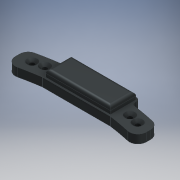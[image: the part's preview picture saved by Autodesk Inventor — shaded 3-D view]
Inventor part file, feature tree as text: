
AUTODESK INVENTOR PART (.ipt)
format: ipt  version: 2018 (Build 220112000, 112)  size: 166,400 bytes
history: native  units: mm
features: extrude x2, sketch x2, hole x1, mirror x1, fillet x1
ambient origin geometry x8: Origin, YZ Plane, XZ Plane, XY Plane, X Axis, Y Axis, Z Axis, Center Point
bodies: Solid1 (feature_tree)
feature tree (7):
  extrude  "Extrusion1"  Depth=77.0mm
  sketch  "Sketch2"  dims[d6=38.5mm d9=5.0mm d10=2.0mm d11=5.0mm d12=0.0mm d13=38.0mm d14=15.0mm d15=1.0mm d16=25.0mm d17=31.0mm d18=3.0mm d19=3.0mm d20=5.0mm d21=1.5mm d22=4.0mm d23=0.0mm d24=3.0mm d25=6.0mm d26=6.0mm d27=2.0mm d28=90.0deg d29=8.0mm d30=20.594885mm d31=2.0mm]
  extrude  "Extrusion2"  Depth=5.0mm
  hole  "Hole1"  [1 undecoded]
  mirror  "Mirror1"
  fillet  "Fillet1"  Radius=5.0mm
  sketch  "Sketch1"  dims[d0=245.0mm d1=10.0mm d3=4.5mm d5=77.0mm]
note: 1 required parameter value undecoded (feature->parameter linkage not recoverable at this tier; creation-order binding heuristic only, values carry confidence <= 0.55)
